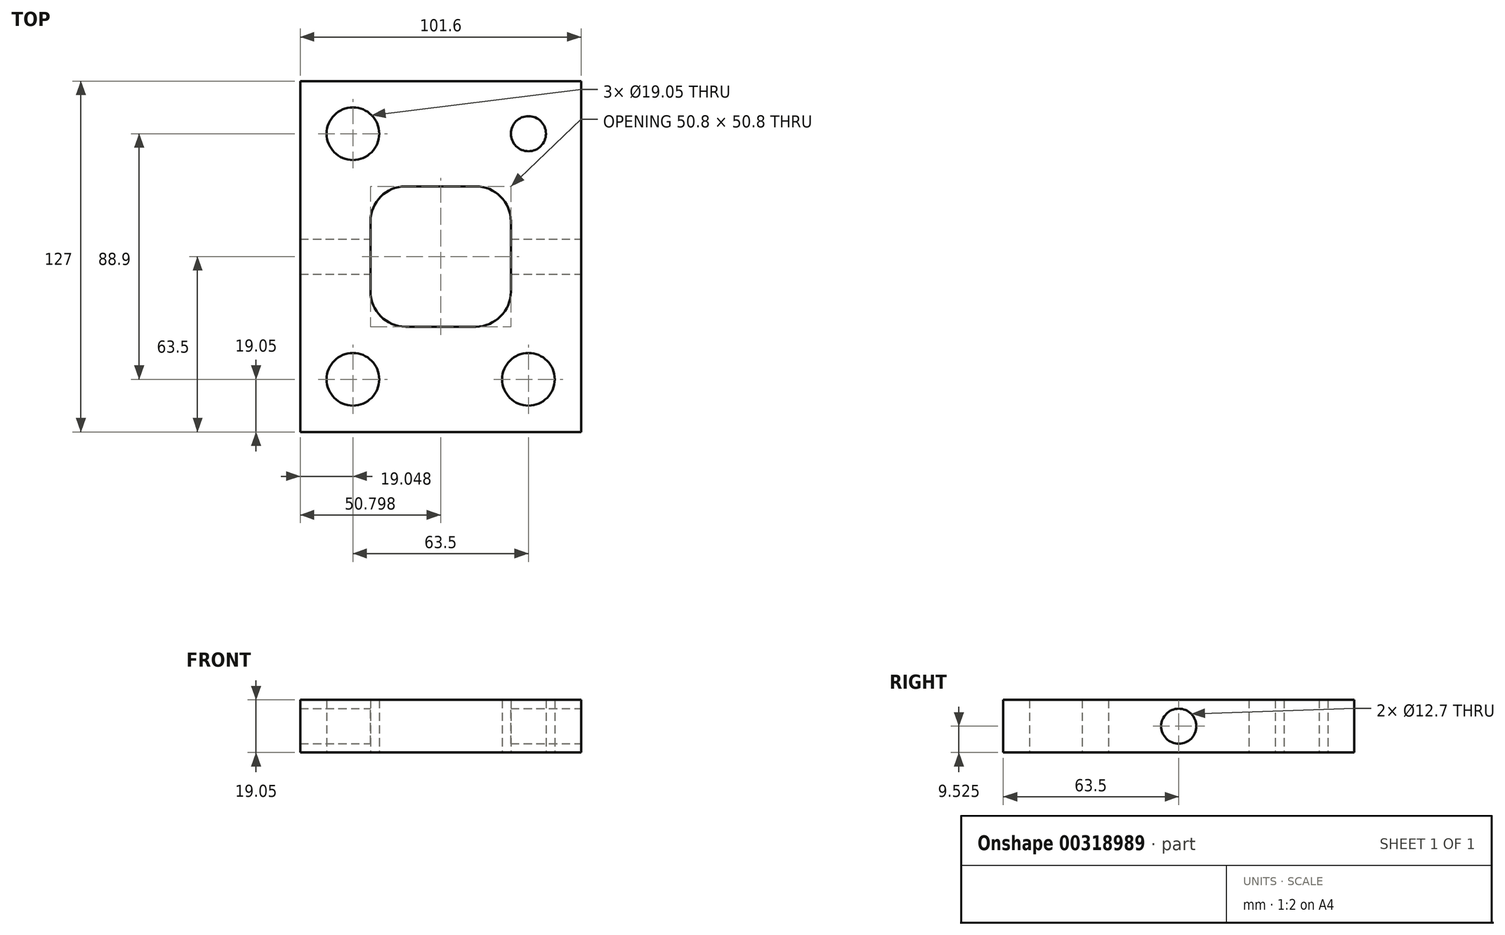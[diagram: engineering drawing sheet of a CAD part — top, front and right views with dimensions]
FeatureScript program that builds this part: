
annotation { "Feature Type Name" : "Feature", "Feature Type Description" : "" }
export const myFeature = defineFeature(function(context is Context, id is Id, definition is map)
    precondition{}
    {
        {
            var Q0;
            Q0=qCreatedBy(makeId("Top.planeOp"),FACE);
            var sketch = newSketch(context, id + "F0", { "sketchPlane" : qUnion([Q0])});
            skLineSegment(sketch, "E0.bottom", {"start": v(-140.78, 63.5) * mm, "end": v(-39.18, 63.5) * mm});
            skLineSegment(sketch, "E0.top", {"start": v(-140.78, -63.5) * mm, "end": v(-39.18, -63.5) * mm});
            skLineSegment(sketch, "E0.left", {"start": v(-140.78, 63.5) * mm, "end": v(-140.78, -63.5) * mm});
            skLineSegment(sketch, "E0.right", {"start": v(-39.18, 63.5) * mm, "end": v(-39.18, -63.5) * mm});
            skLineSegment(sketch, "E1.bottom", {"start": v(-115.38, 25.4) * mm, "end": v(-64.58, 25.4) * mm});
            skLineSegment(sketch, "E1.top", {"start": v(-115.38, -25.4) * mm, "end": v(-64.58, -25.4) * mm});
            skLineSegment(sketch, "E1.left", {"start": v(-115.38, 25.4) * mm, "end": v(-115.38, -25.4) * mm});
            skLineSegment(sketch, "E1.right", {"start": v(-64.58, 25.4) * mm, "end": v(-64.58, -25.4) * mm});
            skCircle(sketch, "E2", {"center": v(-121.73, 44.45) * mm, "radius": 9.53 * mm});
            skCircle(sketch, "E3", {"center": v(-58.23, 44.45) * mm, "radius": 6.35 * mm});
            skCircle(sketch, "E4", {"center": v(-58.23, -44.45) * mm, "radius": 9.53 * mm});
            skCircle(sketch, "E5", {"center": v(-121.73, -44.45) * mm, "radius": 9.53 * mm});
            skPoint(sketch, "E6", {"position": v(-39.18, 0) * mm});
            skPoint(sketch, "E7", {"position": v(-140.78, 0) * mm});
            skSolve(sketch);
        }
        {
            var Q0;
            Q0 = qSketchRegion(id + "F0", true);
            extrude(context, id + "F1", {"entities" : qUnion([Q0]), "depth" : 19.05 * mm});
        }
        {
            var Q0;
            Q0=makeQuery(id+"F1.opExtrude","SWEPT_EDGE",EDGE,{"disambiguationData":[OSD([sQuery(id+"F0.wireOp",EDGE,"E1.top"),sQuery(id+"F0.wireOp",EDGE,"E1.left")])]});
            var Q1;
            Q1=makeQuery(id+"F1.opExtrude","SWEPT_EDGE",EDGE,{"disambiguationData":[OSD([sQuery(id+"F0.wireOp",EDGE,"E1.top"),sQuery(id+"F0.wireOp",EDGE,"E1.right")])]});
            var Q2;
            Q2=makeQuery(id+"F1.opExtrude","SWEPT_EDGE",EDGE,{"disambiguationData":[OSD([sQuery(id+"F0.wireOp",EDGE,"E1.bottom"),sQuery(id+"F0.wireOp",EDGE,"E1.right")])]});
            var Q3;
            Q3=makeQuery(id+"F1.opExtrude","SWEPT_EDGE",EDGE,{"disambiguationData":[OSD([sQuery(id+"F0.wireOp",EDGE,"E1.bottom"),sQuery(id+"F0.wireOp",EDGE,"E1.left")])]});
            fillet(context, id + "F2", {"entities" : qUnion([Q0, Q1, Q2, Q3]), "radius" : 12.7 * mm, "tangentPropagation" : true, "allowEdgeOverflow" : false});
        }
        {
            var Q0;
            Q0=makeQuery(id+"F1.opExtrude","SWEPT_FACE",FACE,{"disambiguationData":[OSD([sQuery(id+"F0.wireOp",EDGE,"E0.right")])]});
            var sketch = newSketch(context, id + "F3", { "sketchPlane" : qUnion([Q0])});
            skCircle(sketch, "E8", {"center": v(0, 9.53) * mm, "radius": 6.35 * mm});
            skSolve(sketch);
        }
        {
            var Q0;
            Q0=makeQuery(id+"F3.imprint","IMPRINT",FACE,{"disambiguationData":[TD([[makeQuery(id+"F3.imprint","IMPRINT",EDGE,{"derivedFrom":sQuery(id+"F3.wireOp",EDGE,"E8")}),1.0]])]});
            extrude(context, id + "F4", {"entities" : qUnion([Q0]), "operationType" : NewBodyOperationType.REMOVE, "endBound" : BoundingType.THROUGH_ALL, "oppositeDirection" : true, "depth" : 25.4 * mm});
        }
    });
